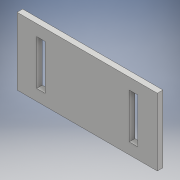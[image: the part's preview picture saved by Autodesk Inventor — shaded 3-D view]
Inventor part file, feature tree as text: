
AUTODESK INVENTOR PART (.ipt)
format: ipt  version: 2017 SP1 (Build 210196100, 196)  size: 108,544 bytes
history: native  units: mm
features: extrude x2, sketch x2
ambient origin geometry x8: Origin, YZ Plane, XZ Plane, XY Plane, X Axis, Y Axis, Z Axis, Center Point
bodies: Solide1 (feature_tree)
feature tree (4):
  extrude  "Extrusion1"  Depth=250.0mm
  extrude  "Extrusion2"  Depth=120.0mm
  sketch  "Esquisse1"
  sketch  "Esquisse2"
